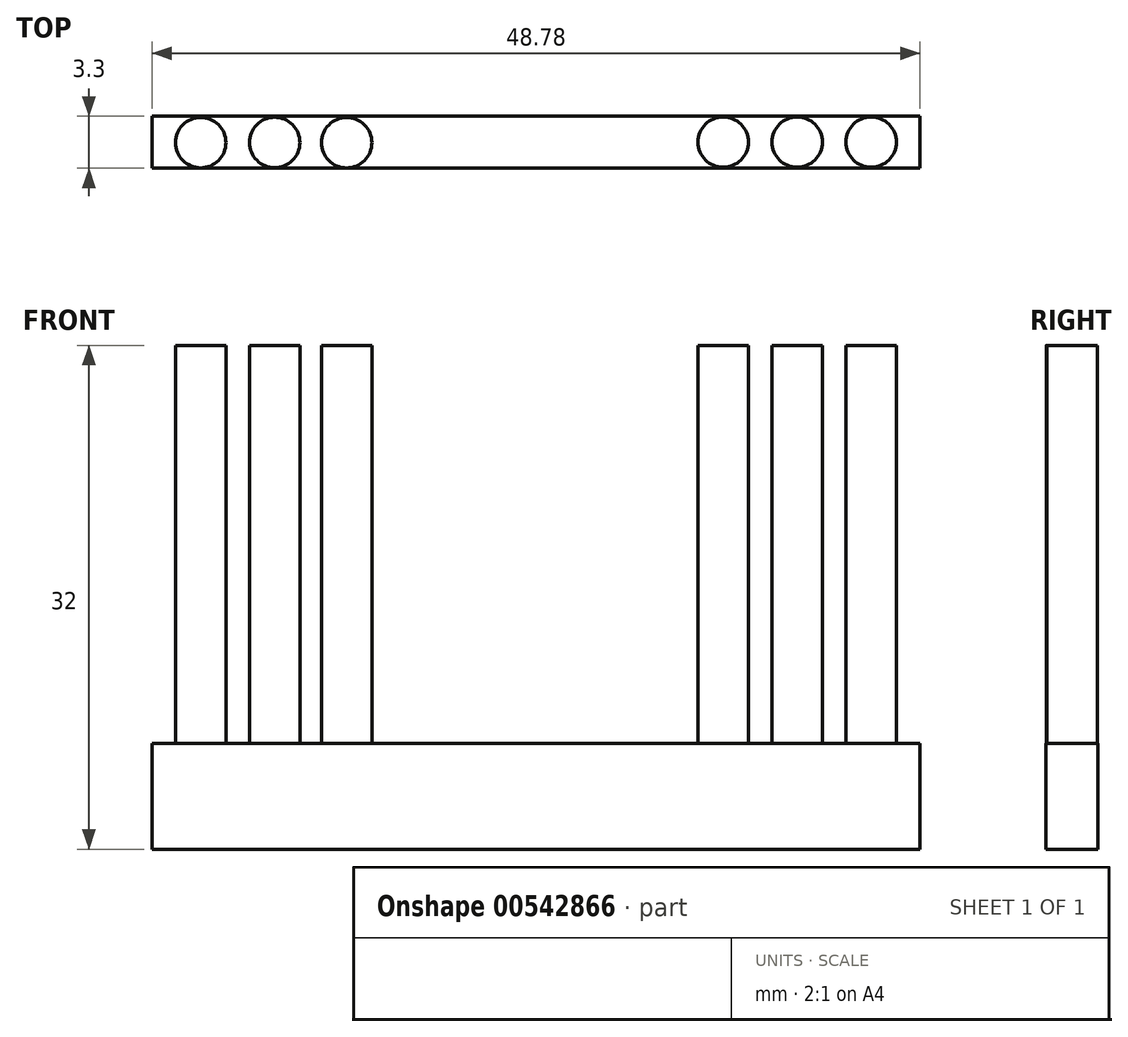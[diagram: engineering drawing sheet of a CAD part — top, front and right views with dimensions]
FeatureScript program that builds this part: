
annotation { "Feature Type Name" : "Feature", "Feature Type Description" : "" }
export const myFeature = defineFeature(function(context is Context, id is Id, definition is map)
    precondition{}
    {
        {
            var Q0;
            Q0=qCreatedBy(makeId("Front.planeOp"),FACE);
            var sketch = newSketch(context, id + "F0", { "sketchPlane" : qUnion([Q0])});
            skLineSegment(sketch, "E0.bottom", {"start": v(0, 0) * mm, "end": v(48.78, 0) * mm});
            skLineSegment(sketch, "E0.top", {"start": v(0, 6.73) * mm, "end": v(48.78, 6.73) * mm});
            skLineSegment(sketch, "E0.left", {"start": v(0, 0) * mm, "end": v(0, 6.73) * mm});
            skLineSegment(sketch, "E0.right", {"start": v(48.78, 0) * mm, "end": v(48.78, 6.73) * mm});
            skSolve(sketch);
        }
        {
            var Q0;
            Q0=makeQuery(id+"F0.imprint","IMPRINT",FACE,{"disambiguationData":[TD([[makeQuery(id+"F0.imprint","IMPRINT",EDGE,{"derivedFrom":sQuery(id+"F0.wireOp",EDGE,"E0.bottom")}),1.0]])]});
            extrude(context, id + "F1", {"entities" : qUnion([Q0]), "oppositeDirection" : true, "depth" : 3.3 * mm, "offsetDistance" : 25.4 * mm});
        }
        {
            var Q0;
            Q0=qCreatedBy(makeId("Top.planeOp"),FACE);
            var sketch = newSketch(context, id + "F2", { "sketchPlane" : qUnion([Q0])});
            skCircle(sketch, "E1", {"center": v(3.1, 1.63) * mm, "radius": 1.6 * mm});
            skCircle(sketch, "E2", {"center": v(7.8, 1.64) * mm, "radius": 1.6 * mm});
            skCircle(sketch, "E3", {"center": v(12.37, 1.62) * mm, "radius": 1.6 * mm});
            skCircle(sketch, "E4", {"center": v(45.68, 1.66) * mm, "radius": 1.6 * mm});
            skCircle(sketch, "E5", {"center": v(40.98, 1.66) * mm, "radius": 1.6 * mm});
            skCircle(sketch, "E6", {"center": v(36.28, 1.66) * mm, "radius": 1.6 * mm});
            skSolve(sketch);
        }
        {
            var Q0;
            Q0=makeQuery(id+"F2.imprint","IMPRINT",FACE,{"disambiguationData":[TD([[makeQuery(id+"F2.imprint","IMPRINT",EDGE,{"derivedFrom":sQuery(id+"F2.wireOp",EDGE,"E1")}),1.0]])]});
            var Q1;
            Q1=makeQuery(id+"F2.imprint","IMPRINT",FACE,{"disambiguationData":[TD([[makeQuery(id+"F2.imprint","IMPRINT",EDGE,{"derivedFrom":sQuery(id+"F2.wireOp",EDGE,"E2")}),1.0]])]});
            var Q2;
            Q2=makeQuery(id+"F2.imprint","IMPRINT",FACE,{"disambiguationData":[TD([[makeQuery(id+"F2.imprint","IMPRINT",EDGE,{"derivedFrom":sQuery(id+"F2.wireOp",EDGE,"E3")}),1.0]])]});
            var Q3;
            Q3=makeQuery(id+"F2.imprint","IMPRINT",FACE,{"disambiguationData":[TD([[makeQuery(id+"F2.imprint","IMPRINT",EDGE,{"derivedFrom":sQuery(id+"F2.wireOp",EDGE,"E6")}),1.0]])]});
            var Q4;
            Q4=makeQuery(id+"F2.imprint","IMPRINT",FACE,{"disambiguationData":[TD([[makeQuery(id+"F2.imprint","IMPRINT",EDGE,{"derivedFrom":sQuery(id+"F2.wireOp",EDGE,"E5")}),1.0]])]});
            var Q5;
            Q5=makeQuery(id+"F2.imprint","IMPRINT",FACE,{"disambiguationData":[TD([[makeQuery(id+"F2.imprint","IMPRINT",EDGE,{"derivedFrom":sQuery(id+"F2.wireOp",EDGE,"E4")}),1.0]])]});
            var Q6;
            Q6=sQuery(id+"F2.wireOp",EDGE,"E1");
            var Q7;
            Q7=sQuery(id+"F2.wireOp",EDGE,"E2");
            var Q8;
            Q8=sQuery(id+"F2.wireOp",EDGE,"E3");
            var Q9;
            Q9=sQuery(id+"F2.wireOp",EDGE,"E6");
            var Q10;
            Q10=sQuery(id+"F2.wireOp",EDGE,"E5");
            var Q11;
            Q11=sQuery(id+"F2.wireOp",EDGE,"E4");
            extrude(context, id + "F3", {"entities" : qUnion([Q0, Q1, Q2, Q3, Q4, Q5]), "operationType" : NewBodyOperationType.ADD, "surfaceEntities" : qUnion([Q6, Q7, Q8, Q9, Q10, Q11]), "depth" : 32 * mm, "offsetDistance" : 25 * mm});
        }
    });
